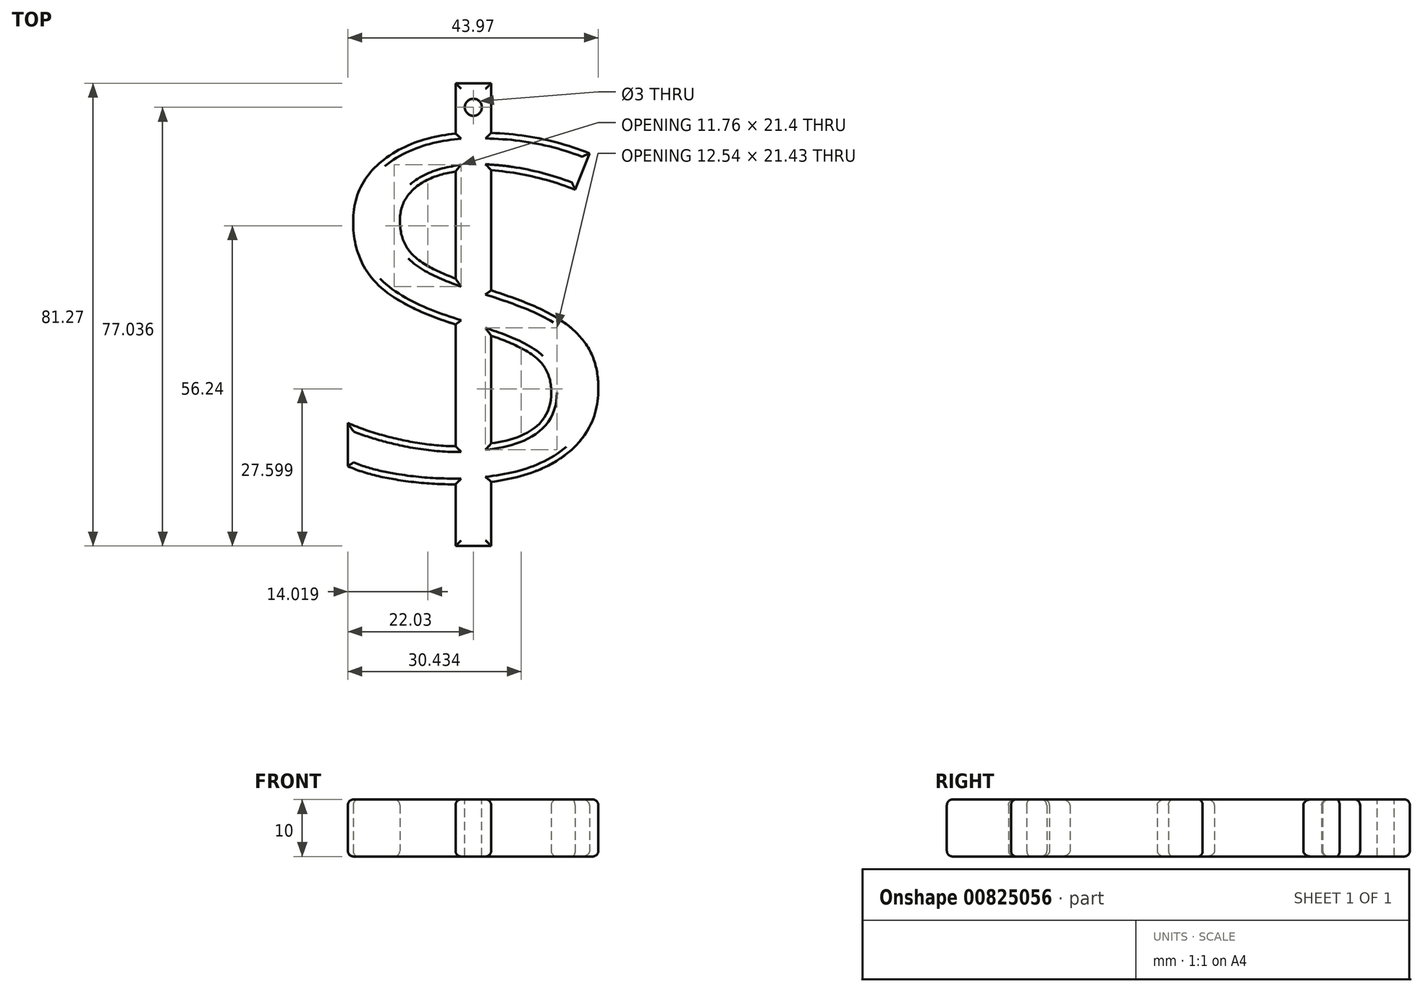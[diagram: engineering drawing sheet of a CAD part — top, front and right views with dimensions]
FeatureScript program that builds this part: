
annotation { "Feature Type Name" : "Feature", "Feature Type Description" : "" }
export const myFeature = defineFeature(function(context is Context, id is Id, definition is map)
    precondition{}
    {
        {
            var Q0;
            Q0=qCreatedBy(makeId("Top.planeOp"),FACE);
            var sketch = newSketch(context, id + "F0", { "sketchPlane" : qUnion([Q0])});
            skText(sketch, "E0", { "text": "$", "fontName": "OpenSans-Regular.ttf"});
            const initialGuessF0  = {"E0": [0, 0, 1, 0, 0.07163]};
            skSetInitialGuess(sketch, initialGuessF0);
            skSolve(sketch);
        }
        {
            var Q0;
            Q0 = qSketchRegion(id + "F0", true);
            extrude(context, id + "F1", {"entities" : qUnion([Q0]), "depth" : 10 * mm, "offsetDistance" : 25 * mm});
        }
        {
            var Q0;
            Q0=makeQuery(id+"F1.opExtrude","CAP_FACE",FACE,{"disambiguationData":[OSD([sQuery(id+"F0.wireOp",EDGE,"E0.sketch_text.stroke-0"),sQuery(id+"F0.wireOp",EDGE,"E0.sketch_text.stroke-1"),sQuery(id+"F0.wireOp",EDGE,"E0.sketch_text.stroke-2"),sQuery(id+"F0.wireOp",EDGE,"E0.sketch_text.stroke-3"),sQuery(id+"F0.wireOp",EDGE,"E0.sketch_text.stroke-4"),sQuery(id+"F0.wireOp",EDGE,"E0.sketch_text.stroke-5"),sQuery(id+"F0.wireOp",EDGE,"E0.sketch_text.stroke-6"),sQuery(id+"F0.wireOp",EDGE,"E0.sketch_text.stroke-7"),sQuery(id+"F0.wireOp",EDGE,"E0.sketch_text.stroke-8"),sQuery(id+"F0.wireOp",EDGE,"E0.sketch_text.stroke-9"),sQuery(id+"F0.wireOp",EDGE,"E0.sketch_text.stroke-10"),sQuery(id+"F0.wireOp",EDGE,"E0.sketch_text.stroke-11"),sQuery(id+"F0.wireOp",EDGE,"E0.sketch_text.stroke-12"),sQuery(id+"F0.wireOp",EDGE,"E0.sketch_text.stroke-13"),sQuery(id+"F0.wireOp",EDGE,"E0.sketch_text.stroke-14"),sQuery(id+"F0.wireOp",EDGE,"E0.sketch_text.stroke-15"),sQuery(id+"F0.wireOp",EDGE,"E0.sketch_text.stroke-16"),sQuery(id+"F0.wireOp",EDGE,"E0.sketch_text.stroke-17"),sQuery(id+"F0.wireOp",EDGE,"E0.sketch_text.stroke-18"),sQuery(id+"F0.wireOp",EDGE,"E0.sketch_text.stroke-19"),sQuery(id+"F0.wireOp",EDGE,"E0.sketch_text.stroke-20"),sQuery(id+"F0.wireOp",EDGE,"E0.sketch_text.stroke-21"),sQuery(id+"F0.wireOp",EDGE,"E0.sketch_text.stroke-22"),sQuery(id+"F0.wireOp",EDGE,"E0.sketch_text.stroke-23"),sQuery(id+"F0.wireOp",EDGE,"E0.sketch_text.stroke-24"),sQuery(id+"F0.wireOp",EDGE,"E0.sketch_text.stroke-25"),sQuery(id+"F0.wireOp",EDGE,"E0.sketch_text.stroke-26"),sQuery(id+"F0.wireOp",EDGE,"E0.sketch_text.stroke-27"),sQuery(id+"F0.wireOp",EDGE,"E0.sketch_text.stroke-28"),sQuery(id+"F0.wireOp",EDGE,"E0.sketch_text.stroke-29"),sQuery(id+"F0.wireOp",EDGE,"E0.sketch_text.stroke-30"),sQuery(id+"F0.wireOp",EDGE,"E0.sketch_text.stroke-31"),sQuery(id+"F0.wireOp",EDGE,"E0.sketch_text.stroke-32"),sQuery(id+"F0.wireOp",EDGE,"E0.sketch_text.stroke-33")])],"isStart":false});
            fillet(context, id + "F2", {"entities" : qUnion([Q0]), "radius" : 1 * mm, "tangentPropagation" : true, "allowEdgeOverflow" : false});
        }
        {
            var Q0;
            Q0=makeQuery(id+"F1.opExtrude","CAP_FACE",FACE,{"disambiguationData":[OSD([sQuery(id+"F0.wireOp",EDGE,"E0.sketch_text.stroke-0"),sQuery(id+"F0.wireOp",EDGE,"E0.sketch_text.stroke-1"),sQuery(id+"F0.wireOp",EDGE,"E0.sketch_text.stroke-2"),sQuery(id+"F0.wireOp",EDGE,"E0.sketch_text.stroke-3"),sQuery(id+"F0.wireOp",EDGE,"E0.sketch_text.stroke-4"),sQuery(id+"F0.wireOp",EDGE,"E0.sketch_text.stroke-5"),sQuery(id+"F0.wireOp",EDGE,"E0.sketch_text.stroke-6"),sQuery(id+"F0.wireOp",EDGE,"E0.sketch_text.stroke-7"),sQuery(id+"F0.wireOp",EDGE,"E0.sketch_text.stroke-8"),sQuery(id+"F0.wireOp",EDGE,"E0.sketch_text.stroke-9"),sQuery(id+"F0.wireOp",EDGE,"E0.sketch_text.stroke-10"),sQuery(id+"F0.wireOp",EDGE,"E0.sketch_text.stroke-11"),sQuery(id+"F0.wireOp",EDGE,"E0.sketch_text.stroke-12"),sQuery(id+"F0.wireOp",EDGE,"E0.sketch_text.stroke-13"),sQuery(id+"F0.wireOp",EDGE,"E0.sketch_text.stroke-14"),sQuery(id+"F0.wireOp",EDGE,"E0.sketch_text.stroke-15"),sQuery(id+"F0.wireOp",EDGE,"E0.sketch_text.stroke-16"),sQuery(id+"F0.wireOp",EDGE,"E0.sketch_text.stroke-17"),sQuery(id+"F0.wireOp",EDGE,"E0.sketch_text.stroke-18"),sQuery(id+"F0.wireOp",EDGE,"E0.sketch_text.stroke-19"),sQuery(id+"F0.wireOp",EDGE,"E0.sketch_text.stroke-20"),sQuery(id+"F0.wireOp",EDGE,"E0.sketch_text.stroke-21"),sQuery(id+"F0.wireOp",EDGE,"E0.sketch_text.stroke-22"),sQuery(id+"F0.wireOp",EDGE,"E0.sketch_text.stroke-23"),sQuery(id+"F0.wireOp",EDGE,"E0.sketch_text.stroke-24"),sQuery(id+"F0.wireOp",EDGE,"E0.sketch_text.stroke-25"),sQuery(id+"F0.wireOp",EDGE,"E0.sketch_text.stroke-26"),sQuery(id+"F0.wireOp",EDGE,"E0.sketch_text.stroke-27"),sQuery(id+"F0.wireOp",EDGE,"E0.sketch_text.stroke-28"),sQuery(id+"F0.wireOp",EDGE,"E0.sketch_text.stroke-29"),sQuery(id+"F0.wireOp",EDGE,"E0.sketch_text.stroke-30"),sQuery(id+"F0.wireOp",EDGE,"E0.sketch_text.stroke-31"),sQuery(id+"F0.wireOp",EDGE,"E0.sketch_text.stroke-32"),sQuery(id+"F0.wireOp",EDGE,"E0.sketch_text.stroke-33")])],"isStart":true});
            fillet(context, id + "F3", {"entities" : qUnion([Q0]), "radius" : 1 * mm, "tangentPropagation" : true, "allowEdgeOverflow" : false});
        }
        {
            var Q0;
            Q0=makeQuery(id+"F1.opExtrude","CAP_FACE",FACE,{"disambiguationData":[OSD([sQuery(id+"F0.wireOp",EDGE,"E0.sketch_text.stroke-0"),sQuery(id+"F0.wireOp",EDGE,"E0.sketch_text.stroke-1"),sQuery(id+"F0.wireOp",EDGE,"E0.sketch_text.stroke-2"),sQuery(id+"F0.wireOp",EDGE,"E0.sketch_text.stroke-3"),sQuery(id+"F0.wireOp",EDGE,"E0.sketch_text.stroke-4"),sQuery(id+"F0.wireOp",EDGE,"E0.sketch_text.stroke-5"),sQuery(id+"F0.wireOp",EDGE,"E0.sketch_text.stroke-6"),sQuery(id+"F0.wireOp",EDGE,"E0.sketch_text.stroke-7"),sQuery(id+"F0.wireOp",EDGE,"E0.sketch_text.stroke-8"),sQuery(id+"F0.wireOp",EDGE,"E0.sketch_text.stroke-9"),sQuery(id+"F0.wireOp",EDGE,"E0.sketch_text.stroke-10"),sQuery(id+"F0.wireOp",EDGE,"E0.sketch_text.stroke-11"),sQuery(id+"F0.wireOp",EDGE,"E0.sketch_text.stroke-12"),sQuery(id+"F0.wireOp",EDGE,"E0.sketch_text.stroke-13"),sQuery(id+"F0.wireOp",EDGE,"E0.sketch_text.stroke-14"),sQuery(id+"F0.wireOp",EDGE,"E0.sketch_text.stroke-15"),sQuery(id+"F0.wireOp",EDGE,"E0.sketch_text.stroke-16"),sQuery(id+"F0.wireOp",EDGE,"E0.sketch_text.stroke-17"),sQuery(id+"F0.wireOp",EDGE,"E0.sketch_text.stroke-18"),sQuery(id+"F0.wireOp",EDGE,"E0.sketch_text.stroke-19"),sQuery(id+"F0.wireOp",EDGE,"E0.sketch_text.stroke-20"),sQuery(id+"F0.wireOp",EDGE,"E0.sketch_text.stroke-21"),sQuery(id+"F0.wireOp",EDGE,"E0.sketch_text.stroke-22"),sQuery(id+"F0.wireOp",EDGE,"E0.sketch_text.stroke-23"),sQuery(id+"F0.wireOp",EDGE,"E0.sketch_text.stroke-24"),sQuery(id+"F0.wireOp",EDGE,"E0.sketch_text.stroke-25"),sQuery(id+"F0.wireOp",EDGE,"E0.sketch_text.stroke-26"),sQuery(id+"F0.wireOp",EDGE,"E0.sketch_text.stroke-27"),sQuery(id+"F0.wireOp",EDGE,"E0.sketch_text.stroke-28"),sQuery(id+"F0.wireOp",EDGE,"E0.sketch_text.stroke-29"),sQuery(id+"F0.wireOp",EDGE,"E0.sketch_text.stroke-30"),sQuery(id+"F0.wireOp",EDGE,"E0.sketch_text.stroke-31"),sQuery(id+"F0.wireOp",EDGE,"E0.sketch_text.stroke-32"),sQuery(id+"F0.wireOp",EDGE,"E0.sketch_text.stroke-33")])],"isStart":false});
            var sketch = newSketch(context, id + "F4", { "sketchPlane" : qUnion([Q0])});
            skCircle(sketch, "E1", {"center": v(28.4, 71.26) * mm, "radius": 1.5 * mm});
            skPoint(sketch, "E1.centerSnap0", {"position": v(26.26, 70.12) * mm});
            skPoint(sketch, "E1.centerSnap1", {"position": v(28.4, 74.48) * mm});
            skSolve(sketch);
        }
        {
            var Q0;
            Q0 = qSketchRegion(id + "F4", true);
            extrude(context, id + "F5", {"entities" : qUnion([Q0]), "operationType" : NewBodyOperationType.REMOVE, "oppositeDirection" : true, "depth" : 10 * mm, "offsetDistance" : 25 * mm});
        }
    });
